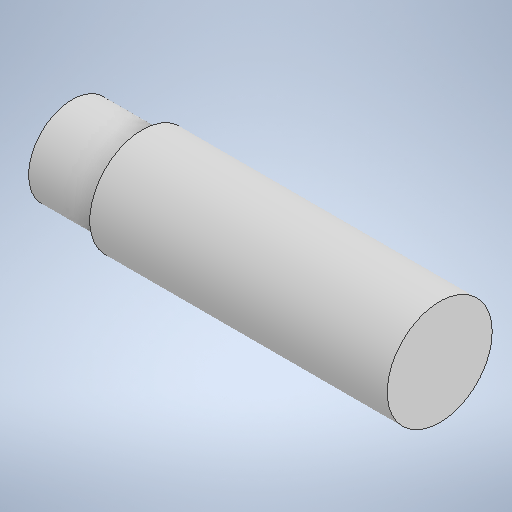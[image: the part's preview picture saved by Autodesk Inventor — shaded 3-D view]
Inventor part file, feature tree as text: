
AUTODESK INVENTOR PART (.ipt)
format: ipt  version: 2025.1 (Build 291241000, 241)  size: 231,936 bytes
history: native  units: mm
features: revolve x1, sketch x1
ambient origin geometry x8: Origin, YZ Plane, XZ Plane, XY Plane, X Axis, Y Axis, Z Axis, Center Point
bodies: Solid1 (feature_tree)
feature tree (2):
  revolve  "Revolution1"  [1 undecoded]
  sketch  "Sketch1"  dims[d0=21.0mm d1=4.0mm d2=5.0mm d3=6.0mm d4=90.0deg]
note: 1 required parameter value undecoded (feature->parameter linkage not recoverable at this tier; creation-order binding heuristic only, values carry confidence <= 0.55)
